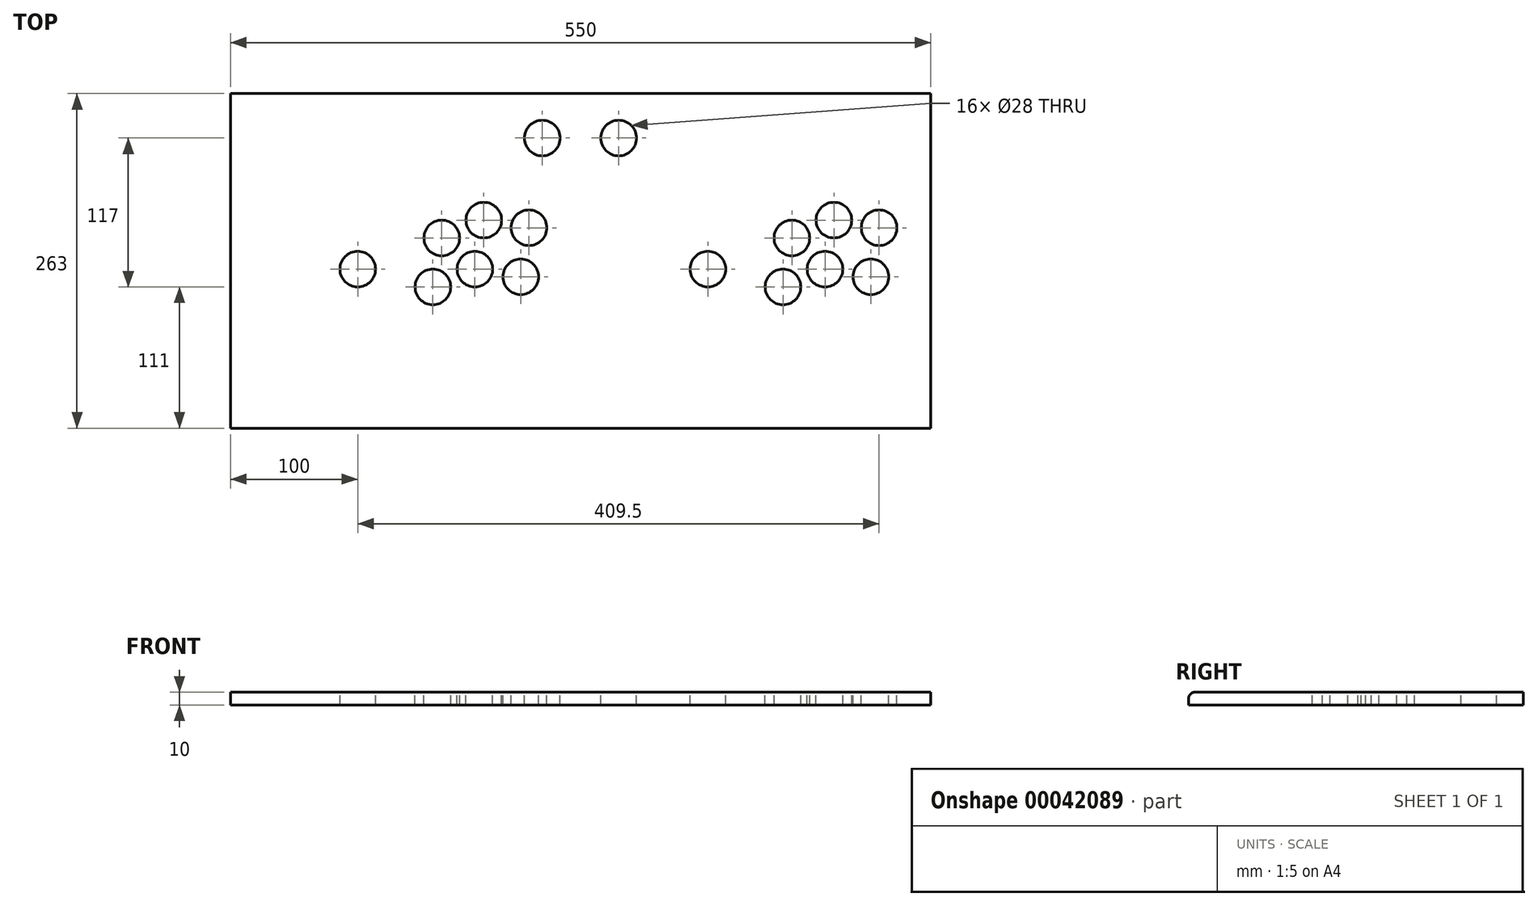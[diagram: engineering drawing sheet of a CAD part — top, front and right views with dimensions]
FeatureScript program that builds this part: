
annotation { "Feature Type Name" : "Feature", "Feature Type Description" : "" }
export const myFeature = defineFeature(function(context is Context, id is Id, definition is map)
    precondition{}
    {
        {
            var Q0;
            Q0=qCreatedBy(makeId("Top.planeOp"),FACE);
            var sketch = newSketch(context, id + "F0", { "sketchPlane" : qUnion([Q0])});
            skLineSegment(sketch, "E0.rect.bottom", {"start": v(275, -131.5) * mm, "end": v(-275, -131.5) * mm});
            skLineSegment(sketch, "E0.rect.top", {"start": v(275, 131.5) * mm, "end": v(-275, 131.5) * mm});
            skLineSegment(sketch, "E0.rect.left", {"start": v(275, -131.5) * mm, "end": v(275, 131.5) * mm});
            skLineSegment(sketch, "E0.rect.right", {"start": v(-275, -131.5) * mm, "end": v(-275, 131.5) * mm});
            skPoint(sketch, "E0.rect.middle", {"position": v(0, 0) * mm});
            skLineSegment(sketch, "E1", {"start": v(-175, 126.17) * mm, "end": v(-175, -128.01) * mm, "construction": true});
            skLineSegment(sketch, "E2", {"start": v(-283.54, -6.5) * mm, "end": v(283.75, -6.5) * mm, "construction": true});
            skCircle(sketch, "E3", {"center": v(-175, -6.5) * mm, "radius": 14 * mm});
            skLineSegment(sketch, "E4", {"start": v(0, 124.53) * mm, "end": v(0, -126.37) * mm, "construction": true});
            skLineSegment(sketch, "E5", {"start": v(-283, 96.5) * mm, "end": v(283.75, 96.5) * mm, "construction": true});
            skCircle(sketch, "E6", {"center": v(-30, 96.5) * mm, "radius": 14 * mm});
            skLineSegment(sketch, "E7", {"start": v(-116, 112.17) * mm, "end": v(-116, -140.92) * mm, "construction": true});
            skLineSegment(sketch, "E8", {"start": v(-109, 112.17) * mm, "end": v(-109, -142.01) * mm, "construction": true});
            skLineSegment(sketch, "E9", {"start": v(-83, 112.17) * mm, "end": v(-83, -142.01) * mm, "construction": true});
            skLineSegment(sketch, "E10", {"start": v(-76, 112.17) * mm, "end": v(-76, -142.01) * mm, "construction": true});
            skLineSegment(sketch, "E11", {"start": v(-47, 112.17) * mm, "end": v(-47, -140.92) * mm, "construction": true});
            skLineSegment(sketch, "E12", {"start": v(-40.5, 112.17) * mm, "end": v(-40.5, -141.47) * mm, "construction": true});
            skLineSegment(sketch, "E13", {"start": v(-282.45, -20.5) * mm, "end": v(283.75, -20.5) * mm, "construction": true});
            skLineSegment(sketch, "E14", {"start": v(-285.73, 18) * mm, "end": v(283.75, 18) * mm, "construction": true});
            skLineSegment(sketch, "E15", {"start": v(-283, 32) * mm, "end": v(283.75, 32) * mm, "construction": true});
            skCircle(sketch, "E16", {"center": v(-116, -20.5) * mm, "radius": 14 * mm});
            skCircle(sketch, "E17", {"center": v(-109, 18) * mm, "radius": 14 * mm});
            skCircle(sketch, "E18", {"center": v(-83, -6.5) * mm, "radius": 14 * mm});
            skCircle(sketch, "E19", {"center": v(-76, 32) * mm, "radius": 14 * mm});
            skLineSegment(sketch, "E20", {"start": v(-309.1, -12.5) * mm, "end": v(269.22, -12.5) * mm, "construction": true});
            skCircle(sketch, "E21", {"center": v(-47, -12.5) * mm, "radius": 14 * mm});
            skLineSegment(sketch, "E22", {"start": v(-284.09, 26) * mm, "end": v(283.75, 26) * mm, "construction": true});
            skCircle(sketch, "E23", {"center": v(-40.5, 26) * mm, "radius": 14 * mm});
            skCircle(sketch, "E24.1.0.0", {"center": v(100, -6.5) * mm, "radius": 14 * mm});
            skCircle(sketch, "E24.1.0.1", {"center": v(159, -20.5) * mm, "radius": 14 * mm});
            skCircle(sketch, "E24.1.0.2", {"center": v(166, 18) * mm, "radius": 14 * mm});
            skCircle(sketch, "E24.1.0.3", {"center": v(199, 32) * mm, "radius": 14 * mm});
            skCircle(sketch, "E24.1.0.4", {"center": v(234.5, 26) * mm, "radius": 14 * mm});
            skCircle(sketch, "E24.1.0.5", {"center": v(228, -12.5) * mm, "radius": 14 * mm});
            skCircle(sketch, "E24.1.0.6", {"center": v(192, -6.5) * mm, "radius": 14 * mm});
            skLineSegment(sketch, "E24.direction1", {"start": v(-175, -6.5) * mm, "end": v(100, -6.5) * mm, "construction": true});
            skCircle(sketch, "E25", {"center": v(30, 96.5) * mm, "radius": 14 * mm});
            skSolve(sketch);
        }
        {
            var Q0;
            Q0=makeQuery(id+"F0.imprint","IMPRINT",FACE,{"disambiguationData":[TD([[makeQuery(id+"F0.imprint","IMPRINT",EDGE,{"derivedFrom":sQuery(id+"F0.wireOp",EDGE,"E0.rect.bottom")}),-1.0]])]});
            extrude(context, id + "F1", {"entities" : qUnion([Q0]), "oppositeDirection" : true, "depth" : 10 * mm});
        }
        {
            var Q0;
            Q0=makeQuery(id+"F1.opExtrude","CAP_EDGE",EDGE,{"disambiguationData":[OSD([sQuery(id+"F0.wireOp",EDGE,"E0.rect.bottom")])],"isStart":true});
            fillet(context, id + "F2", {"entities" : qUnion([Q0]), "radius" : 5 * mm, "tangentPropagation" : true, "allowEdgeOverflow" : false});
        }
    });
